# Revit family: WBS_AA4110_ES_Breed_Tripple
name_source: partatom
category: Windows
revit_build: Autodesk Revit Architecture 2013 (Build: 20120221_2030(x64)
units: mm (PartAtom-declared; Revit-internal decimal feet)

## types (1)
- Enkel schuivend breed vleugelprofiel tripple glas
    Analytic Construction = <None>
    Assembly Code = B2030110
    Default Sill Height = 0 mm  [stored 0 ft]
    Description = Kawneer Schuifpui AA 4110 Enkelschuivend conform Standaard systeemomschrijving AA4110 (hef)schuifsysteem
    Dikte Stelkozijn = 27 mm  [stored 0.0885827 ft]
    Dikte Stelkozijn onderzijde = 27 mm  [stored 0.0885827 ft]
    DikteStelkozijnOnderzijde_SpelingPui_BuitenbladMWOnderzijde = 17 mm  [stored 0.0557743 ft]
    DikteStelkozijn_SpelingPui_BuitenbladMW = 17 mm  [stored 0.0557743 ft]
    Glasdikte (totaal) = 29 mm  [stored 0.0951444 ft]
    GlassType = Glass, Clear Glazing, Low E
    HalveSpouw = 65 mm  [stored 0.213255 ft]
    HalveSpouw_OffsetVkKozijn_Stelkozijn = 79 mm
    Height = 2620 mm  [stored 8.5958 ft]
    Keynote = 30.33
    Kleur Binnenzijde = Kawneer RAL 9010
    Kleur Binnenzijde Vleugel = Kawneer RAL 9010
    Kleur Buitenzijde = Kawneer RAL 9010
    Kleur Buitenzijde Vleugel = Kawneer RAL 9010
    Kleur H&S = Kawneer Anodiseer kleur RVS-look
    Model = Enkel schuivend breed vleugelprofiel Tripple glazing
    NL-SfB-Code = 31.32.30
    OffsetVkKozijnVkStelkozijn = 14 mm  [stored 0.0459318 ft]
    Speling Pui_ buitenblad MW = 10 mm  [stored 0.0328084 ft]
    Speling Pui_buitenblad MW Onderzijde = 10 mm  [stored 0.0328084 ft]
    Spouwdiepte = 130 mm  [stored 0.426509 ft]
    Type Comments = Vrij te parameteriseren Revit Model
    URL = http://www.kawneer.com
    Wall Closure = By host
    Width = 1800 mm  [stored 5.90551 ft]

note: [stored X ft] marks values corroborated as IEEE doubles in the binary element streams (Revit-internal decimal feet)

## geometry (parser evidence)
native form markers: Blend x12, Sweep x48
no freeform markers — native parametric forms only
